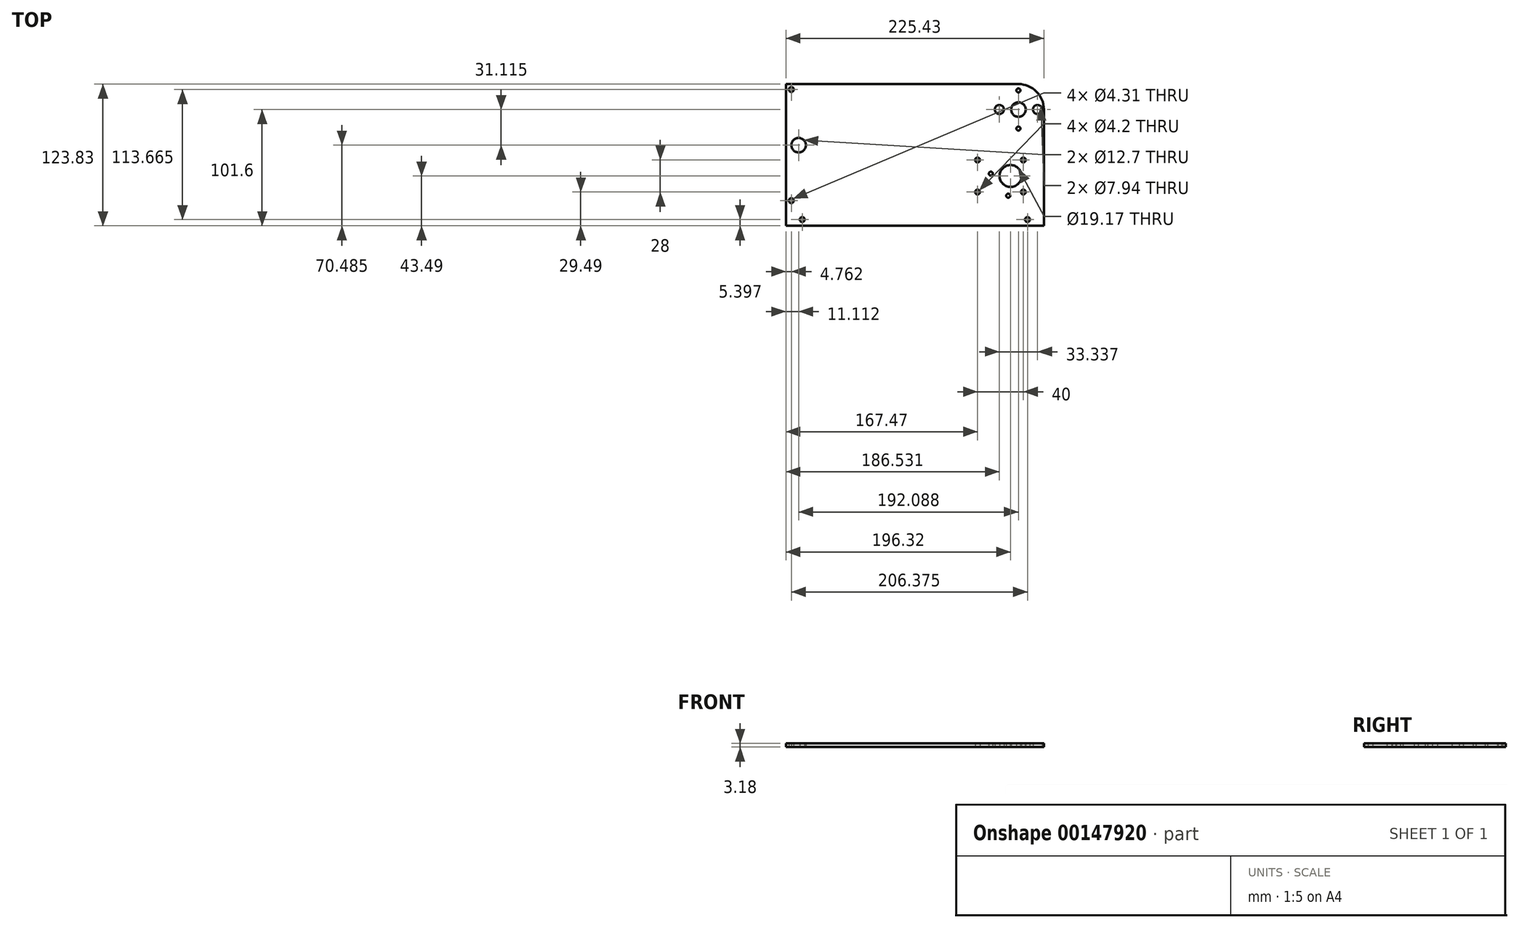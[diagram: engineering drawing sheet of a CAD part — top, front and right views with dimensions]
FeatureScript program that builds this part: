
annotation { "Feature Type Name" : "Feature", "Feature Type Description" : "" }
export const myFeature = defineFeature(function(context is Context, id is Id, definition is map)
    precondition{}
    {
        {
            var Q0;
            Q0=qCreatedBy(makeId("Top.planeOp"),FACE);
            var sketch = newSketch(context, id + "F0", { "sketchPlane" : qUnion([Q0])});
            skCircle(sketch, "E0", {"center": v(0, 0) * mm, "radius": 6.35 * mm});
            skCircle(sketch, "E1", {"center": v(0, 16.67) * mm, "radius": 5.56 * mm, "construction": true});
            skCircle(sketch, "E2", {"center": v(0, 16.67) * mm, "radius": 1.73 * mm});
            skCircle(sketch, "E3", {"center": v(0, -16.67) * mm, "radius": 1.73 * mm});
            skLineSegment(sketch, "E4.bottom", {"start": v(-203.2, 22.22) * mm, "end": v(0, 22.23) * mm});
            skLineSegment(sketch, "E4.top", {"start": v(-203.2, -101.6) * mm, "end": v(22.23, -101.6) * mm});
            skLineSegment(sketch, "E4.left", {"start": v(-203.2, 22.22) * mm, "end": v(-203.2, -101.6) * mm});
            skLineSegment(sketch, "E5.bottom", {"start": v(0, 16.67) * mm, "end": v(16.67, 0) * mm, "construction": true});
            skLineSegment(sketch, "E5.top", {"start": v(-16.67, 0) * mm, "end": v(0, -16.67) * mm, "construction": true});
            skLineSegment(sketch, "E5.left", {"start": v(0, 16.67) * mm, "end": v(-16.67, 0) * mm, "construction": true});
            skLineSegment(sketch, "E5.right", {"start": v(16.67, 0) * mm, "end": v(0, -16.67) * mm, "construction": true});
            skCircle(sketch, "E6", {"center": v(-16.67, 0) * mm, "radius": 3.97 * mm});
            skCircle(sketch, "E7", {"center": v(16.67, 0) * mm, "radius": 3.97 * mm});
            skArc(sketch, "E8", {"start": v(22.23, 0) * mm, "mid": v(15.72, 15.72) * mm, "end": v(0, 22.23) * mm});
            skLineSegment(sketch, "E9", {"start": v(22.23, -101.6) * mm, "end": v(22.23, -90.8) * mm});
            skLineSegment(sketch, "E10", {"start": v(22.23, -90.8) * mm, "end": v(22.23, 0) * mm});
            skLineSegment(sketch, "E11", {"start": v(0, 0) * mm, "end": v(0, -101.6) * mm, "construction": true});
            skLineSegment(sketch, "E12", {"start": v(22.23, -96.2) * mm, "end": v(7.94, -96.2) * mm, "construction": true});
            skCircle(sketch, "E13", {"center": v(7.94, -96.2) * mm, "radius": 2.15 * mm});
            skLineSegment(sketch, "E14", {"start": v(-198.44, 22.22) * mm, "end": v(-198.44, 17.46) * mm, "construction": true});
            skLineSegment(sketch, "E15", {"start": v(-203.2, -96.2) * mm, "end": v(-188.91, -96.2) * mm, "construction": true});
            skCircle(sketch, "E16", {"center": v(-188.91, -96.2) * mm, "radius": 2.15 * mm});
            skCircle(sketch, "E17", {"center": v(-198.44, 17.46) * mm, "radius": 2.15 * mm});
            skLineSegment(sketch, "E18", {"start": v(-198.44, -79.7) * mm, "end": v(-198.44, 17.46) * mm, "construction": true});
            skLineSegment(sketch, "E19", {"start": v(-198.44, -79.7) * mm, "end": v(-198.44, -96.2) * mm, "construction": true});
            skCircle(sketch, "E20", {"center": v(-198.44, -79.7) * mm, "radius": 2.15 * mm});
            skLineSegment(sketch, "E21.bottom", {"start": v(-35.73, -44.11) * mm, "end": v(4.27, -44.11) * mm, "construction": true});
            skLineSegment(sketch, "E21.top", {"start": v(-35.73, -72.11) * mm, "end": v(4.27, -72.11) * mm, "construction": true});
            skLineSegment(sketch, "E21.left", {"start": v(-35.73, -44.11) * mm, "end": v(-35.73, -72.11) * mm, "construction": true});
            skLineSegment(sketch, "E21.right", {"start": v(4.27, -44.11) * mm, "end": v(4.27, -72.11) * mm, "construction": true});
            skLineSegment(sketch, "E22", {"start": v(4.27, -58.11) * mm, "end": v(-6.88, -58.11) * mm, "construction": true});
            skCircle(sketch, "E23", {"center": v(-6.88, -58.11) * mm, "radius": 9.59 * mm});
            skCircle(sketch, "E24", {"center": v(-35.73, -44.11) * mm, "radius": 2.1 * mm});
            skCircle(sketch, "E25", {"center": v(-35.73, -72.11) * mm, "radius": 2.1 * mm});
            skCircle(sketch, "E26", {"center": v(4.27, -72.11) * mm, "radius": 2.1 * mm});
            skCircle(sketch, "E27", {"center": v(4.27, -44.11) * mm, "radius": 2.1 * mm});
            skLineSegment(sketch, "E28", {"start": v(0, 0) * mm, "end": v(-6.88, -58.11) * mm, "construction": true});
            skCircle(sketch, "E29", {"center": v(-6.88, -58.11) * mm, "radius": 12.6 * mm, "construction": true});
            skLineSegment(sketch, "E30", {"start": v(-6.88, -58.11) * mm, "end": v(-16.52, -65.7) * mm, "construction": true});
            skLineSegment(sketch, "E31", {"start": v(-24.12, -56.07) * mm, "end": v(-8.92, -75.35) * mm, "construction": true});
            skLineSegment(sketch, "E32", {"start": v(-6.88, -58.11) * mm, "end": v(-8.92, -75.35) * mm, "construction": true});
            skCircle(sketch, "E33", {"center": v(-8.92, -75.35) * mm, "radius": 4.76 * mm, "construction": true});
            skCircle(sketch, "E34", {"center": v(-24.12, -56.07) * mm, "radius": 1.73 * mm});
            skCircle(sketch, "E35", {"center": v(-8.92, -75.35) * mm, "radius": 1.73 * mm});
            skLineSegment(sketch, "E36", {"start": v(-198.44, 17.46) * mm, "end": v(-203.2, 17.46) * mm, "construction": true});
            skLineSegment(sketch, "E37", {"start": v(-198.44, -31.12) * mm, "end": v(-192.09, -31.12) * mm, "construction": true});
            skCircle(sketch, "E38", {"center": v(-192.09, -31.12) * mm, "radius": 6.35 * mm});
            skSolve(sketch);
        }
        {
            var Q0;
            Q0=qSketchRegion(id+"F0",true);
            extrude(context, id + "F1", {"entities" : qUnion([Q0]), "depth" : 3.17 * mm});
        }
    });
